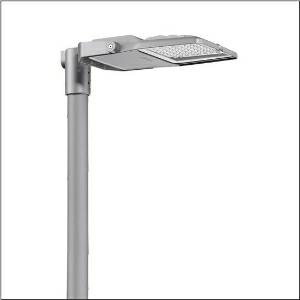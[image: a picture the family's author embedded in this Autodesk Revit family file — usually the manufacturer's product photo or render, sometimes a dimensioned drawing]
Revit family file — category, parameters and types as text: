
# Revit family: floodlight_fl_21_mini___pl64_5xa7775c2e3a_8880
name_source: partatom
category: Lighting Fixtures
units: mm (PartAtom-declared; Revit-internal decimal feet)

## family parameters
Cut with Voids When Loaded = No
Host = Face
Light Source = No
Part Type = Normal
Room Calculation Point = No
Round Connector Dimension = Use Diameter
Shared = No

## types (1)
- --- (1 x LED, 11770 lm, 89 W, 3000K)
    Apparent Load = 89 VA
    CIE Flux Codes = 28 80 98 100 100
    Color Rendering = 70
    Color Temperature = 3000K
    Default Elevation = 1800 mm
    Description = Floodlight FL 21 mini, floodlight, primary light control with lens, of PMMA, primary optical cover: protective disc, of toughened safety glass, transparent, light distribution: PL64, light emission: direct distribution, installation type: surface-mounted, LED, High Power LED, rated luminous flux: 11.770lm, luminous efficacy: 132lm/W, light colour: 730, colour temperature: 3000K, control gear: Smart Interface (Zhaga), control: flexible luminous flux parameterisation, time-dependent luminous flux control, constant luminous flux control, overheat protection, pre-setting: logarithmic dimming characteristic, with terminal, 6-pole, mains connection: 220..240V, AC, 50/60Hz, start of lifetime: 89W, end of service life: 94W, reduction: 43W, luminaire housing, of diecast aluminium, powder-coated, Siteco® metallic grey (DB 702S), corrosivity category C5 mid according to DIN EN ISO 12944, suitable for swimming pools, chlorine-resistant, sealing non-destructively replaceable, please order mast flange separately, mast bracket, of steel, galvanised, powder-coated, Siteco® metallic grey (DB 702S), Smart Interface above, protection rating (complete): IP66, insulation class (complete): insulation class II (safety insulation), certification: CE, ENEC, VDE, protection symbol: D, impact resistance: IK08, permissible operating ambient temperature: -40..+40°C, permissible operating ambient temperature for outdoor applications: -40..+50°C, standard: DIN EN 12944, LABS conformity tested according to VDMA 24364:2018-05, packaging unit: 1 piece

Light Distribution: PL64
    Height = 70 mm
    Lamp = 1 x LED
    Lamp Light Flux = 11770 lm
    Lamp Power = 89 W
    Lamp count = 1
    Length = 485 mm
    Luminous efficacy = 132 lm/W
    Manufacturer = Siteco
    ModVariant = No
    Model = 5XA7775C2E3A
    Number of Poles = 1
    OnlyDefault = Yes
    Power Factor = 1
    Product Name = Floodlight FL 21 mini | PL64
    Product group = floodlight | pylon annexe
    ProductGroupID = 6200
    Protection Class = Protection class II
    Protection Degree = IP 66
    RLX_Detail_Level = 1
    RLX_Emergency_Light_Flux = 0 lm
    RLX_Emergency_Type = 0
    RLX_Emergency_Type_DB = No
    RlxData = <blob elided: 101033 chars, md5=020447f2>
    Socket = socket
    Standby Power = 0 W
    System Light Flux = 11770 lm
    System Power = 89 W
    Type Comments = factory setting: luminous flux: 100 % | dim-lin: 254 | 456 mA
    Type Image = l_1007125.jpg
    URL = http://relux.com
    VarID = @adj_165412
    Voltage = 0 V
    Weight = 0.00 kg
    Width = 337 mm

## geometry (parser evidence)
native form markers: Blend x4, Sweep x12
no freeform markers — native parametric forms only
